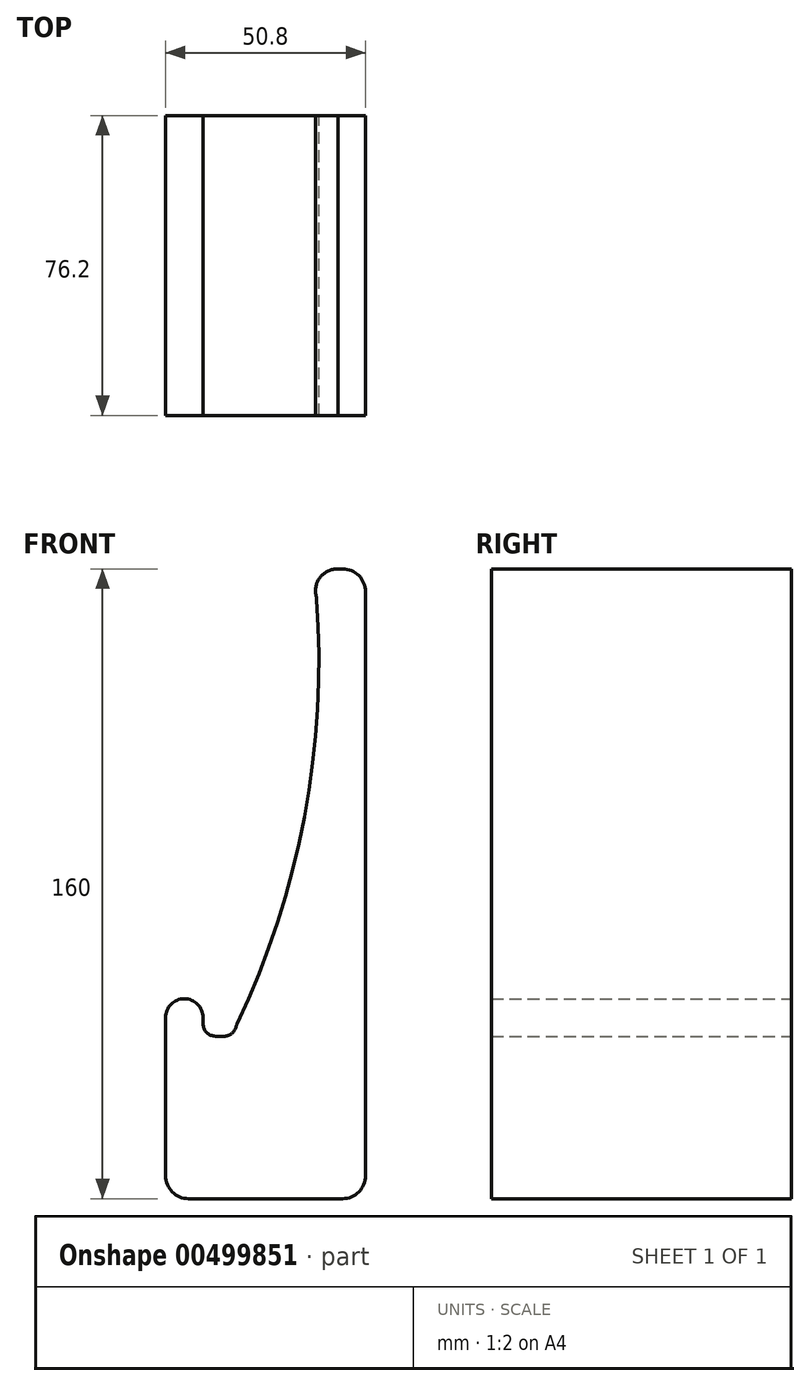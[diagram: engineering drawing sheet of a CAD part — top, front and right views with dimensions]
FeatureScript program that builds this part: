
annotation { "Feature Type Name" : "Feature", "Feature Type Description" : "" }
export const myFeature = defineFeature(function(context is Context, id is Id, definition is map)
    precondition{}
    {
        {
            var Q0;
            Q0=qCreatedBy(makeId("Front.planeOp"),FACE);
            var sketch = newSketch(context, id + "F0", { "sketchPlane" : qUnion([Q0])});
            skLineSegment(sketch, "E0", {"start": v(-25.4, -74.16) * mm, "end": v(-25.4, -33.97) * mm});
            skLineSegment(sketch, "E1", {"start": v(-15.88, -33.97) * mm, "end": v(-15.88, -35.55) * mm});
            skLineSegment(sketch, "E2", {"start": v(-12.7, -38.73) * mm, "end": v(-10.6, -38.73) * mm});
            skLineSegment(sketch, "E3", {"start": v(25.4, -74.16) * mm, "end": v(25.4, 74.16) * mm});
            skLineSegment(sketch, "E4", {"start": v(18.36, 80) * mm, "end": v(19.56, 80) * mm});
            skArc(sketch, "E5", {"start": v(-15.88, -35.55) * mm, "mid": v(-14.95, -37.8) * mm, "end": v(-12.7, -38.73) * mm});
            skArc(sketch, "E6", {"start": v(-10.6, -38.73) * mm, "mid": v(-8.69, -38.1) * mm, "end": v(-7.55, -36.45) * mm});
            skArc(sketch, "E7", {"start": v(-20.64, -29.2) * mm, "mid": v(-24, -30.6) * mm, "end": v(-25.4, -33.97) * mm});
            skArc(sketch, "E8", {"start": v(-15.88, -33.97) * mm, "mid": v(-17.27, -30.6) * mm, "end": v(-20.64, -29.2) * mm});
            skArc(sketch, "E9", {"start": v(18.36, 80) * mm, "mid": v(13.93, 77.93) * mm, "end": v(12.84, 73.15) * mm});
            skArc(sketch, "E10", {"start": v(25.4, 74.16) * mm, "mid": v(23.69, 78.3) * mm, "end": v(19.56, 80) * mm});
            skArc(sketch, "E11", {"start": v(-7.22, -35.6) * mm, "mid": v(9.87, 17) * mm, "end": v(12.99, 72.23) * mm});
            skArc(sketch, "E12", {"start": v(12.99, 72.23) * mm, "mid": v(12.93, 72.7) * mm, "end": v(12.84, 73.15) * mm});
            skArc(sketch, "E13", {"start": v(-7.55, -36.45) * mm, "mid": v(-7.4, -36.02) * mm, "end": v(-7.22, -35.6) * mm});
            skLineSegment(sketch, "E14", {"start": v(19.56, -80) * mm, "end": v(-19.56, -80) * mm});
            skArc(sketch, "E15", {"start": v(19.56, -80) * mm, "mid": v(23.69, -78.3) * mm, "end": v(25.4, -74.16) * mm});
            skArc(sketch, "E16", {"start": v(-25.4, -74.16) * mm, "mid": v(-23.69, -78.3) * mm, "end": v(-19.56, -80) * mm});
            skSolve(sketch);
        }
        {
            var Q0;
            Q0 = qSketchRegion(id + "F0", true);
            extrude(context, id + "F1", {"entities" : qUnion([Q0]), "depth" : 76.2 * mm});
        }
    });
